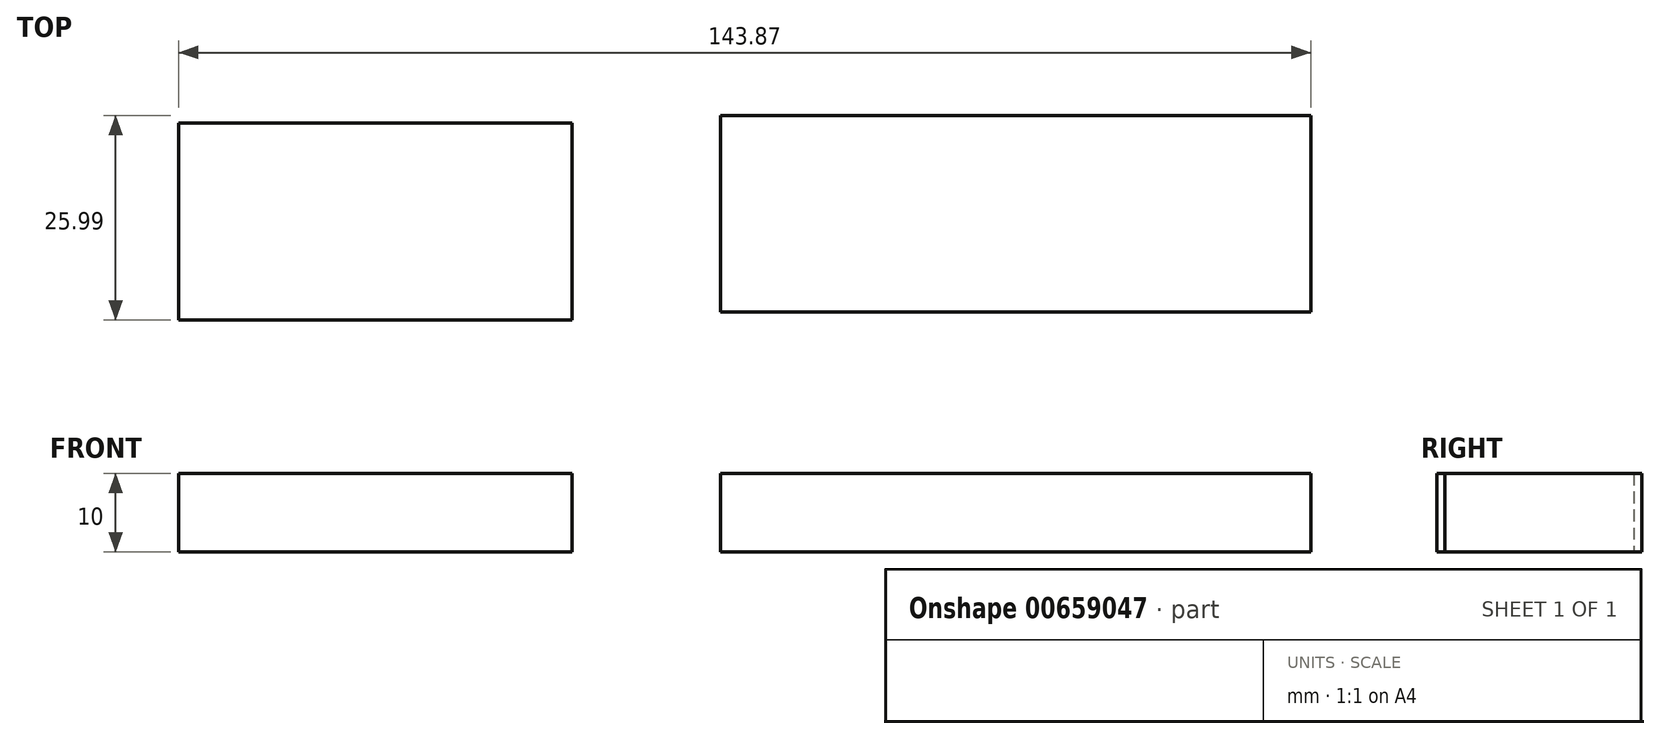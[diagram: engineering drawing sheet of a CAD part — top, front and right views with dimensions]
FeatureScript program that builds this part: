
annotation { "Feature Type Name" : "Feature", "Feature Type Description" : "" }
export const myFeature = defineFeature(function(context is Context, id is Id, definition is map)
    precondition{}
    {
        {
            assignVariable(context, id + "F0", {"name" : "thickness", "anyValue" : 10});
        }
        {
            var Q0;
            Q0=qCreatedBy(makeId("Top.planeOp"),FACE);
            var sketch = newSketch(context, id + "F1", { "sketchPlane" : qUnion([Q0])});
            skLineSegment(sketch, "E0.bottom", {"start": v(-50, 25) * mm, "end": v(0, 25) * mm});
            skLineSegment(sketch, "E0.top", {"start": v(-50, 0) * mm, "end": v(0, 0) * mm});
            skLineSegment(sketch, "E0.left", {"start": v(-50, 25) * mm, "end": v(-50, 0) * mm});
            skLineSegment(sketch, "E0.right", {"start": v(0, 25) * mm, "end": v(0, 0) * mm});
            skSolve(sketch);
        }
        {
            var Q0;
            Q0=makeQuery(id+"F1.imprint","IMPRINT",FACE,{"disambiguationData":[TD([[makeQuery(id+"F1.imprint","IMPRINT",EDGE,{"derivedFrom":sQuery(id+"F1.wireOp",EDGE,"E0.bottom")}),-1.0]])]});
            extrude(context, id + "F2", {"entities" : qUnion([Q0]), "depth" : (getVariable(context, 'thickness')) * mm, "offsetDistance" : 25 * mm});
        }
        {
            var Q0;
            Q0=qCreatedBy(makeId("Top.planeOp"),FACE);
            var sketch = newSketch(context, id + "F3", { "sketchPlane" : qUnion([Q0])});
            skLineSegment(sketch, "E1.bottom", {"start": v(18.87, 26) * mm, "end": v(93.87, 26) * mm});
            skLineSegment(sketch, "E1.top", {"start": v(18.87, 1) * mm, "end": v(93.87, 1) * mm});
            skLineSegment(sketch, "E1.left", {"start": v(18.87, 26) * mm, "end": v(18.87, 1) * mm});
            skLineSegment(sketch, "E1.right", {"start": v(93.87, 26) * mm, "end": v(93.87, 1) * mm});
            skSolve(sketch);
        }
        {
            var Q0;
            Q0=makeQuery(id+"F3.imprint","IMPRINT",FACE,{"disambiguationData":[TD([[makeQuery(id+"F3.imprint","IMPRINT",EDGE,{"derivedFrom":sQuery(id+"F3.wireOp",EDGE,"E1.bottom")}),-1.0]])]});
            extrude(context, id + "F4", {"entities" : qUnion([Q0]), "depth" : (getVariable(context, 'thickness')) * mm, "offsetDistance" : 25 * mm});
        }
    });
